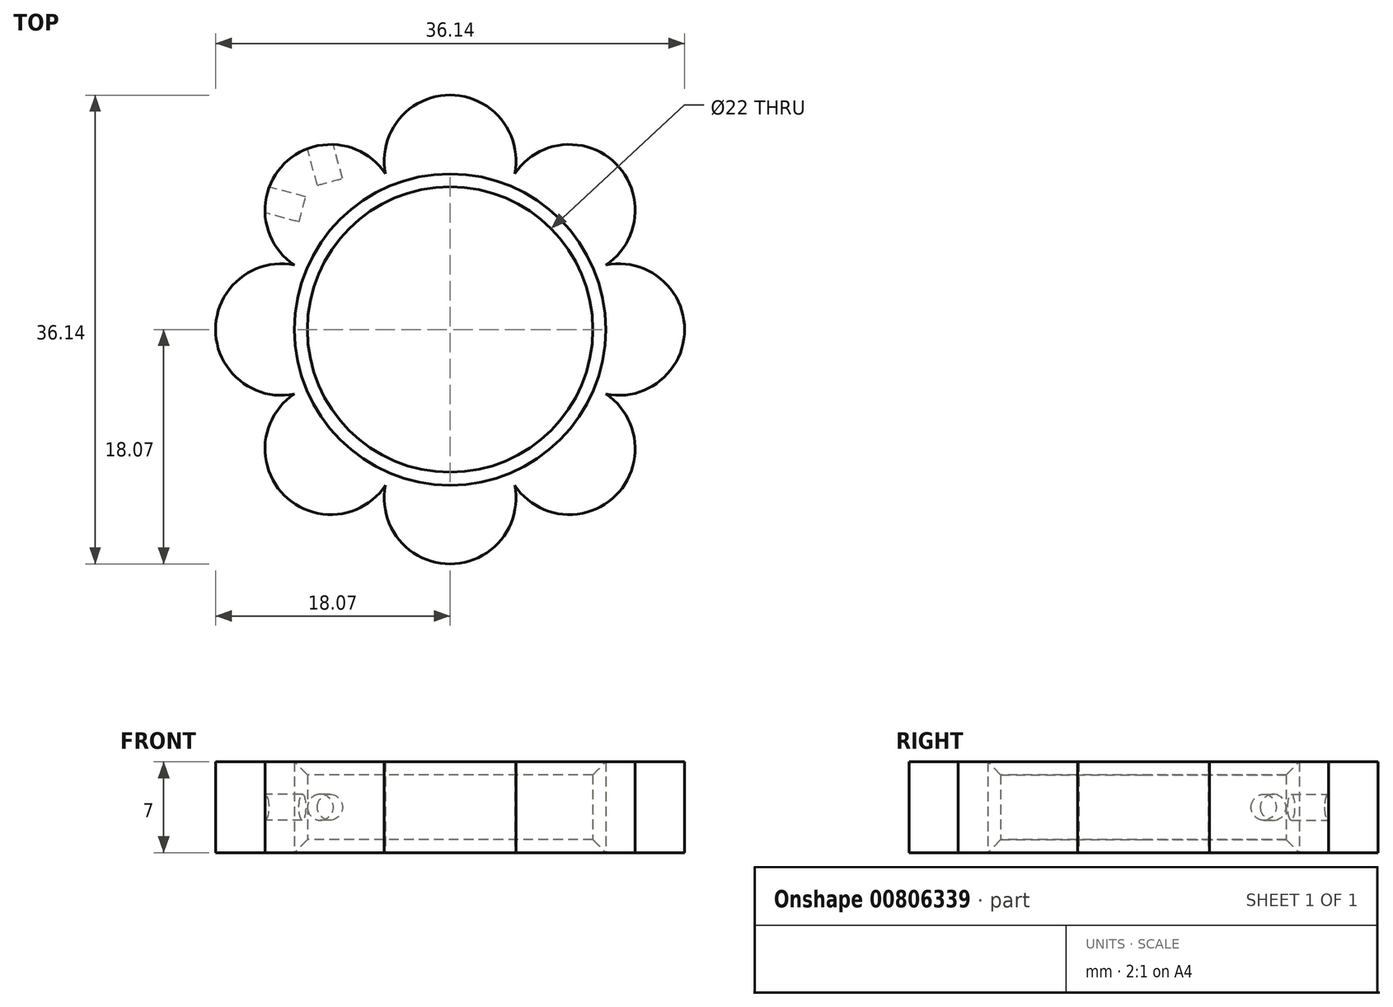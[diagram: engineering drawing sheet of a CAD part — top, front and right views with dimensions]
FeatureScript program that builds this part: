
annotation { "Feature Type Name" : "Feature", "Feature Type Description" : "" }
export const myFeature = defineFeature(function(context is Context, id is Id, definition is map)
    precondition{}
    {
        {
            var Q0;
            Q0=qCreatedBy(makeId("Top.planeOp"),FACE);
            var sketch = newSketch(context, id + "F0", { "sketchPlane" : qUnion([Q0])});
            skCircle(sketch, "E0", {"center": v(0, 0) * mm, "radius": 11 * mm});
            skCircle(sketch, "E1", {"center": v(0, 0) * mm, "radius": 13 * mm});
            skArc(sketch, "E2", {"start": v(4.97, 12.01) * mm, "mid": v(0, 18.07) * mm, "end": v(-4.97, 12.01) * mm});
            skArc(sketch, "E3.1.0", {"start": v(-4.97, 12.01) * mm, "mid": v(-12.78, 12.78) * mm, "end": v(-12.01, 4.97) * mm});
            skArc(sketch, "E3.2.0", {"start": v(-12.01, 4.97) * mm, "mid": v(-18.07, 0) * mm, "end": v(-12.01, -4.97) * mm});
            skArc(sketch, "E3.3.0", {"start": v(-12.01, -4.97) * mm, "mid": v(-12.78, -12.78) * mm, "end": v(-4.97, -12.01) * mm});
            skArc(sketch, "E3.4.0", {"start": v(-4.97, -12.01) * mm, "mid": v(0, -18.07) * mm, "end": v(4.97, -12.01) * mm});
            skArc(sketch, "E3.5.0", {"start": v(4.97, -12.01) * mm, "mid": v(12.78, -12.78) * mm, "end": v(12.01, -4.97) * mm});
            skArc(sketch, "E3.6.0", {"start": v(12.01, -4.97) * mm, "mid": v(18.07, 0) * mm, "end": v(12.01, 4.97) * mm});
            skArc(sketch, "E3.7.0", {"start": v(12.01, 4.97) * mm, "mid": v(12.78, 12.78) * mm, "end": v(4.97, 12.01) * mm});
            skSolve(sketch);
        }
        {
            var Q0;
            Q0 = qSketchRegion(id + "F0", true);
            var Q1;
            Q1=makeQuery(id+"F0.imprint","IMPRINT",FACE,{"disambiguationData":[TD([[makeQuery(id+"F0.imprint","IMPRINT",EDGE,{"derivedFrom":sQuery(id+"F0.wireOp",EDGE,"E0")}),-1.0]])]});
            extrude(context, id + "F1", {"entities" : qUnion([Q0, Q1]), "endBound" : BoundingType.SYMMETRIC, "depth" : 7 * mm, "offsetDistance" : 25 * mm});
        }
        {
            var Q0;
            Q0=makeQuery(id+"F1.opExtrude","CAP_EDGE",EDGE,{"disambiguationData":[OSD([sQuery(id+"F0.wireOp",EDGE,"E0")])],"isStart":false});
            var Q1;
            Q1=makeQuery(id+"F1.opExtrude","CAP_EDGE",EDGE,{"disambiguationData":[OSD([sQuery(id+"F0.wireOp",EDGE,"E0")])],"isStart":true});
            chamfer(context, id + "F2", {"entities" : qUnion([Q0, Q1]), "width" : 1 * mm, "tangentPropagation" : true});
        }
        {
            var Q0;
            Q0=qCreatedBy(makeId("Top.planeOp"),FACE);
            var sketch = newSketch(context, id + "F3", { "sketchPlane" : qUnion([Q0])});
            skLineSegment(sketch, "E4", {"start": v(0, 0) * mm, "end": v(-22.02, 22.02) * mm, "construction": true});
            skLineSegment(sketch, "E5", {"start": v(0, 0) * mm, "end": v(22.02, 22.02) * mm, "construction": true});
            skLineSegment(sketch, "E6", {"start": v(0, 0) * mm, "end": v(22.02, -22.02) * mm, "construction": true});
            skLineSegment(sketch, "E7", {"start": v(0, 0) * mm, "end": v(-22.02, -22.02) * mm, "construction": true});
            skCircle(sketch, "E8.0", {"center": v(0, 0) * mm, "radius": 12 * mm, "construction": true});
            skLineSegment(sketch, "E9", {"start": v(-8.49, 8.49) * mm, "end": v(-11.07, 18.14) * mm, "construction": true});
            skLineSegment(sketch, "E10", {"start": v(-8.49, 8.49) * mm, "end": v(-18.14, 11.07) * mm, "construction": true});
            skSolve(sketch);
        }
        {
            var Q0;
            Q0=sQuery(id+"F3.wireOp",VERTEX,"E9.end");
            var Q1;
            Q1=sQuery(id+"F3.wireOp",EDGE,"E9");
            cPlane(context, id + "F4", {"entities" : qUnion([Q0, Q1]), "cplaneType" : CPlaneType.LINE_POINT, "offset" : 25 * mm, "width" : 150 * mm, "height" : 150 * mm});
        }
        {
            var Q0;
            Q0=sQuery(id+"F3.wireOp",VERTEX,"E10.end");
            var Q1;
            Q1=sQuery(id+"F3.wireOp",EDGE,"E10");
            cPlane(context, id + "F5", {"entities" : qUnion([Q0, Q1]), "cplaneType" : CPlaneType.LINE_POINT, "offset" : 25 * mm, "width" : 150 * mm, "height" : 150 * mm});
        }
        {
            var Q0;
            Q0=qCreatedBy(id+"F4.planeOp",FACE);
            var sketch = newSketch(context, id + "F6", { "sketchPlane" : qUnion([Q0])});
            skPoint(sketch, "E11.0", {"position": v(6, 0) * mm});
            skCircle(sketch, "E12", {"center": v(6, 0) * mm, "radius": 1 * mm});
            skSolve(sketch);
        }
        {
            var Q0;
            Q0 = qSketchRegion(id + "F6", true);
            var Q1;
            Q1=makeQuery(id+"F1.opExtrude","SWEPT_FACE",FACE,{"disambiguationData":[OSD([sQuery(id+"F0.wireOp",EDGE,"E0")])]});
            var Q2;
            Q2=makeQuery(id+"F1.opExtrude","SWEPT_BODY",BODY,{"disambiguationData":[OSD([sQuery(id+"F0.wireOp",EDGE,"E0"),sQuery(id+"F0.wireOp",EDGE,"E2"),sQuery(id+"F0.wireOp",EDGE,"E3.1.0"),sQuery(id+"F0.wireOp",EDGE,"E3.2.0"),sQuery(id+"F0.wireOp",EDGE,"E3.3.0"),sQuery(id+"F0.wireOp",EDGE,"E3.4.0"),sQuery(id+"F0.wireOp",EDGE,"E3.5.0"),sQuery(id+"F0.wireOp",EDGE,"E3.6.0"),sQuery(id+"F0.wireOp",EDGE,"E3.7.0")])]});
            extrude(context, id + "F7", {"entities" : qUnion([Q0]), "operationType" : NewBodyOperationType.REMOVE, "oppositeDirection" : true, "depth" : 7 * mm, "endBoundEntityFace" : qUnion([Q1]), "endBoundEntityBody" : qUnion([Q2]), "offsetDistance" : 25 * mm});
        }
        {
            var Q0;
            Q0=qCreatedBy(makeId("Right.planeOp"),FACE);
            var sketch = newSketch(context, id + "F8", { "sketchPlane" : qUnion([Q0])});
            skLineSegment(sketch, "E13", {"start": v(0, 0) * mm, "end": v(0, -23.6) * mm, "construction": true});
            skSolve(sketch);
        }
        {
            var Q0;
            Q0=qCreatedBy(id+"F5.planeOp",FACE);
            var sketch = newSketch(context, id + "F9", { "sketchPlane" : qUnion([Q0])});
            skPoint(sketch, "E14.0", {"position": v(-6, 0) * mm});
            skCircle(sketch, "E15", {"center": v(-6, 0) * mm, "radius": 1 * mm});
            skSolve(sketch);
        }
        {
            var Q0;
            Q0 = qSketchRegion(id + "F9", true);
            var Q1;
            Q1=makeQuery(id+"F1.opExtrude","SWEPT_FACE",FACE,{"disambiguationData":[OSD([sQuery(id+"F0.wireOp",EDGE,"E0")])]});
            extrude(context, id + "F10", {"entities" : qUnion([Q0]), "operationType" : NewBodyOperationType.REMOVE, "oppositeDirection" : true, "depth" : 7 * mm, "endBoundEntityFace" : qUnion([Q1]), "offsetDistance" : 25 * mm});
        }
    });
